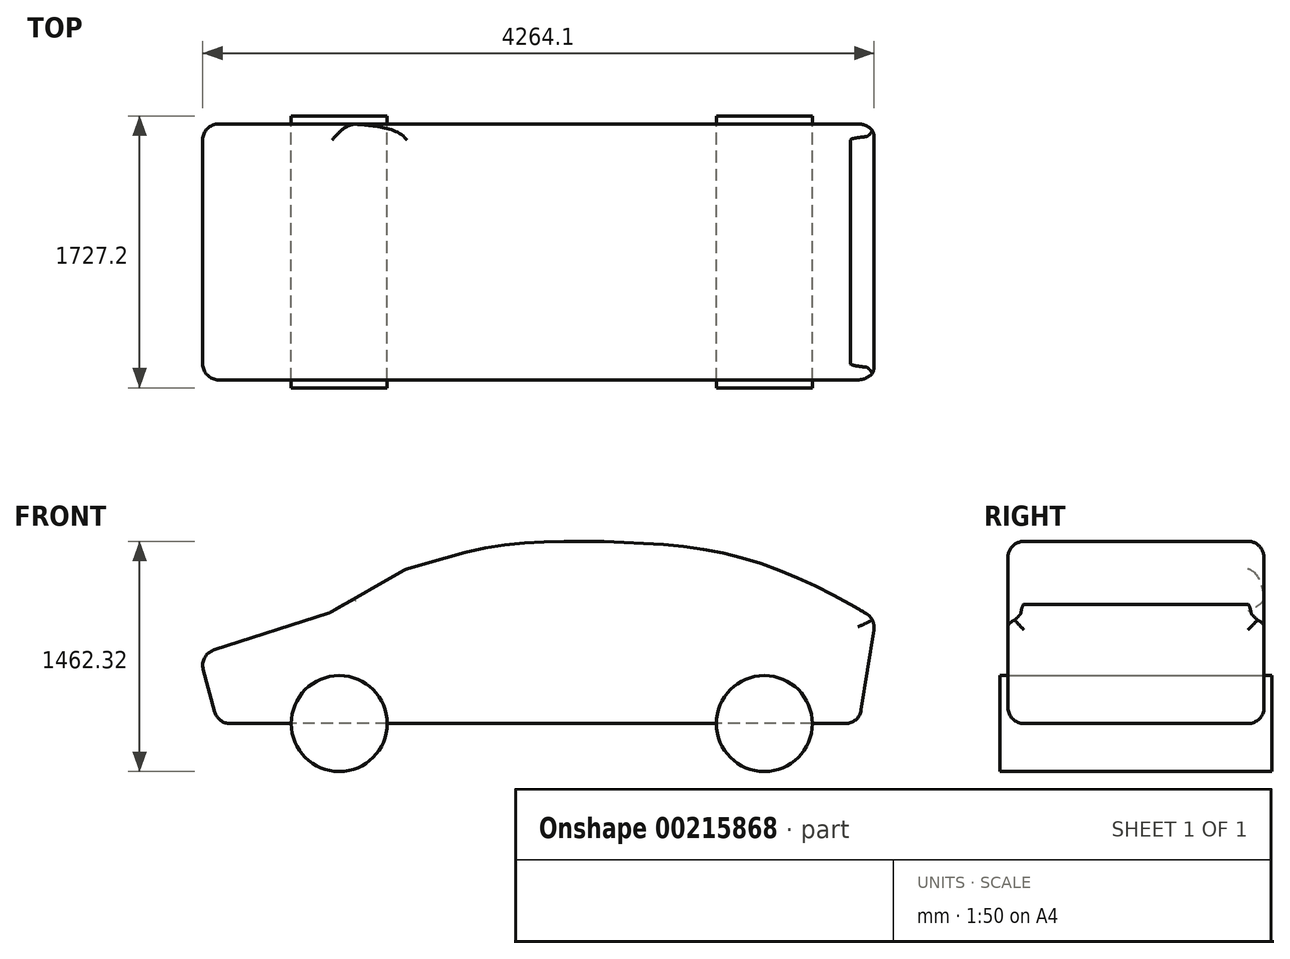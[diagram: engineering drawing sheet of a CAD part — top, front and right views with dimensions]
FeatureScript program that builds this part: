
annotation { "Feature Type Name" : "Feature", "Feature Type Description" : "" }
export const myFeature = defineFeature(function(context is Context, id is Id, definition is map)
    precondition{}
    {
        {
            var Q0;
            Q0=qCreatedBy(makeId("Front.planeOp"),FACE);
            var sketch = newSketch(context, id + "F0", { "sketchPlane" : qUnion([Q0])});
            skCircle(sketch, "E0", {"center": v(0, 0) * mm, "radius": 304.8 * mm});
            skCircle(sketch, "E1", {"center": v(-2700.02, 0) * mm, "radius": 304.8 * mm});
            skSolve(sketch);
        }
        {
            var Q0;
            Q0=makeQuery(id+"F0.imprint","IMPRINT",FACE,{"disambiguationData":[TD([[makeQuery(id+"F0.imprint","IMPRINT",EDGE,{"derivedFrom":sQuery(id+"F0.wireOp",EDGE,"E1")}),1.0]])]});
            var Q1;
            Q1=makeQuery(id+"F0.imprint","IMPRINT",FACE,{"disambiguationData":[TD([[makeQuery(id+"F0.imprint","IMPRINT",EDGE,{"derivedFrom":sQuery(id+"F0.wireOp",EDGE,"E0")}),1.0]])]});
            extrude(context, id + "F1", {"entities" : qUnion([Q0, Q1]), "endBound" : BoundingType.SYMMETRIC, "depth" : 1727.2 * mm});
        }
        {
            var Q0;
            Q0=qCreatedBy(makeId("Front.planeOp"),FACE);
            var sketch = newSketch(context, id + "F2", { "sketchPlane" : qUnion([Q0])});
            skLineSegment(sketch, "E2", {"start": v(601.62, 0) * mm, "end": v(-3470.3, 0) * mm});
            skLineSegment(sketch, "E3", {"start": v(601.62, 0) * mm, "end": v(706.47, 663.66) * mm});
            skLineSegment(sketch, "E4", {"start": v(706.47, 663.66) * mm, "end": v(547.84, 757.19) * mm});
            skLineSegment(sketch, "E5", {"start": v(-3470.3, 0) * mm, "end": v(-3589.02, 436.47) * mm});
            skLineSegment(sketch, "E6", {"start": v(-3589.02, 436.47) * mm, "end": v(-2753.79, 707.35) * mm});
            skLineSegment(sketch, "E7", {"start": v(-2753.79, 707.35) * mm, "end": v(-2281.93, 978.23) * mm});
            skFitSpline(sketch, "E8", {"points": [v(-2281.93, 978.23) * mm, v(-1547.9, 1144.67) * mm, v(-739.73, 1143.57) * mm, v(547.84, 757.19) * mm], "startDerivative": vector(3921.87, 1177.64) * mm, "endDerivative": vector(4147.64, -2340.14) * mm});
            skLineSegment(sketch, "E9", {"start": v(-5722.07, 1211.58) * mm, "end": v(2466.7, 1211.58) * mm, "construction": true});
            skLineSegment(sketch, "E10", {"start": v(855.98, -714.29) * mm, "end": v(855.98, 3066.57) * mm, "construction": true});
            skLineSegment(sketch, "E11", {"start": v(-3589.02, -714.29) * mm, "end": v(-3589.02, 2550.16) * mm, "construction": true});
            skLineSegment(sketch, "E12", {"start": v(2235.45, -279.4) * mm, "end": v(-5145.93, -279.4) * mm, "construction": true});
            skPoint(sketch, "E13.orphan", {"position": v(1008.27, 0) * mm});
            skSolve(sketch);
        }
        {
            var Q0;
            Q0=makeQuery(id+"F2.imprint","IMPRINT",FACE,{"disambiguationData":[TD([[makeQuery(id+"F2.imprint","IMPRINT",EDGE,{"derivedFrom":sQuery(id+"F2.wireOp",EDGE,"E2")}),-1.0]])]});
            extrude(context, id + "F3", {"entities" : qUnion([Q0]), "endBound" : BoundingType.SYMMETRIC, "depth" : 1625.6 * mm});
        }
        {
            var Q0;
            Q0=makeQuery(id+"F3.opExtrude","CAP_EDGE",EDGE,{"disambiguationData":[OSD([sQuery(id+"F2.wireOp",EDGE,"E8")])],"isStart":false});
            var Q1;
            Q1=makeQuery(id+"F3.opExtrude","CAP_EDGE",EDGE,{"disambiguationData":[OSD([sQuery(id+"F2.wireOp",EDGE,"E7")])],"isStart":false});
            var Q2;
            Q2=makeQuery(id+"F3.opExtrude","CAP_EDGE",EDGE,{"disambiguationData":[OSD([sQuery(id+"F2.wireOp",EDGE,"E6")])],"isStart":false});
            var Q3;
            Q3=makeQuery(id+"F3.opExtrude","SWEPT_EDGE",EDGE,{"disambiguationData":[OSD([sQuery(id+"F2.wireOp",EDGE,"E5"),sQuery(id+"F2.wireOp",EDGE,"E6")])]});
            var Q4;
            Q4=makeQuery(id+"F3.opExtrude","SWEPT_EDGE",EDGE,{"disambiguationData":[OSD([sQuery(id+"F2.wireOp",EDGE,"E6"),sQuery(id+"F2.wireOp",EDGE,"E7")])]});
            var Q5;
            Q5=makeQuery(id+"F3.opExtrude","SWEPT_EDGE",EDGE,{"disambiguationData":[OSD([sQuery(id+"F2.wireOp",EDGE,"E7"),sQuery(id+"F2.wireOp",EDGE,"E8")])]});
            var Q6;
            Q6=makeQuery(id+"F3.opExtrude","CAP_EDGE",EDGE,{"disambiguationData":[OSD([sQuery(id+"F2.wireOp",EDGE,"E3")])],"isStart":false});
            var Q7;
            Q7=makeQuery(id+"F3.opExtrude","CAP_EDGE",EDGE,{"disambiguationData":[OSD([sQuery(id+"F2.wireOp",EDGE,"E2")])],"isStart":false});
            var Q8;
            Q8=makeQuery(id+"F3.opExtrude","CAP_EDGE",EDGE,{"disambiguationData":[OSD([sQuery(id+"F2.wireOp",EDGE,"E5")])],"isStart":false});
            var Q9;
            Q9=makeQuery(id+"F3.opExtrude","SWEPT_EDGE",EDGE,{"disambiguationData":[OSD([sQuery(id+"F2.wireOp",EDGE,"E2"),sQuery(id+"F2.wireOp",EDGE,"E5")])]});
            var Q10;
            Q10=makeQuery(id+"F3.opExtrude","CAP_EDGE",EDGE,{"disambiguationData":[OSD([sQuery(id+"F2.wireOp",EDGE,"E5")])],"isStart":true});
            var Q11;
            Q11=makeQuery(id+"F3.opExtrude","CAP_EDGE",EDGE,{"disambiguationData":[OSD([sQuery(id+"F2.wireOp",EDGE,"E6")])],"isStart":true});
            var Q12;
            Q12=makeQuery(id+"F3.opExtrude","CAP_EDGE",EDGE,{"disambiguationData":[OSD([sQuery(id+"F2.wireOp",EDGE,"E2")])],"isStart":true});
            var Q13;
            Q13=makeQuery(id+"F3.opExtrude","CAP_EDGE",EDGE,{"disambiguationData":[OSD([sQuery(id+"F2.wireOp",EDGE,"E8")])],"isStart":true});
            var Q14;
            Q14=makeQuery(id+"F3.opExtrude","CAP_EDGE",EDGE,{"disambiguationData":[OSD([sQuery(id+"F2.wireOp",EDGE,"E3")])],"isStart":true});
            var Q15;
            Q15=makeQuery(id+"F3.opExtrude","SWEPT_EDGE",EDGE,{"disambiguationData":[OSD([sQuery(id+"F2.wireOp",EDGE,"E3"),sQuery(id+"F2.wireOp",EDGE,"E4")])]});
            var Q16;
            Q16=makeQuery(id+"F3.opExtrude","SWEPT_EDGE",EDGE,{"disambiguationData":[OSD([sQuery(id+"F2.wireOp",EDGE,"E2"),sQuery(id+"F2.wireOp",EDGE,"E3")])]});
            fillet(context, id + "F4", {"entities" : qUnion([Q0, Q1, Q2, Q3, Q4, Q5, Q6, Q7, Q8, Q9, Q10, Q11, Q12, Q13, Q14, Q15, Q16]), "radius" : 101.6 * mm, "tangentPropagation" : true, "allowEdgeOverflow" : false});
        }
    });
